# Revit family: SNL
name_source: partatom
category: Lighting Fixtures
revit_build: Autodesk Revit 2013 (Build: 20130531_2115(x64)
units: mm (PartAtom-declared; Revit-internal decimal feet)

## types (2) — shared parameters
Apparent Load = 111 VA
Certifications = CSA listed for U.S. & Canada. Tested to UL 1598 & UL 8750 standards
Color Filter = 16777215
Default Elevation = 48"
Description = LED Sanitube Food Service Strip
Dimming Lamp Color Temperature Shift = <None>
Glass = Hubbell - White Glass
Housing Material = Steel - Hubbell
Lamp = LEDs
Load Classification = Lighting
Manufacturer = Hubbell Industrial Lighting
Manufacturer Fax = 866-898-0131
Model = SNL
Nominal Watts = 100 W
Photometric Web File = generic.ies
Photometric Web Link = http://cdn.hubbellindustrial.com
Power Factor = 0.9
Product Documentation Link = http://cdn.hubbellindustrial.com
Product Page URL = http://www.hubbellindustrial.com
Tilt Angle = -90.00°
URL = http://www.hubbellindustrial.com
Voltage = 120 V
Warranty = Five year warranty
Wattage Comments = 100W

## per-type parameters (varying)
| type | Assembly Code | Emit from Line Length | Weight | zz Length 1 |
| SNL-4 | D5020200 | 48" | 0.01 kip | 48" |
| SNL-8 | D5020 | 96" | 0.02 kip | 96" |

## geometry (parser evidence)
native form markers: Blend x4, Sweep x1
no freeform markers — native parametric forms only
